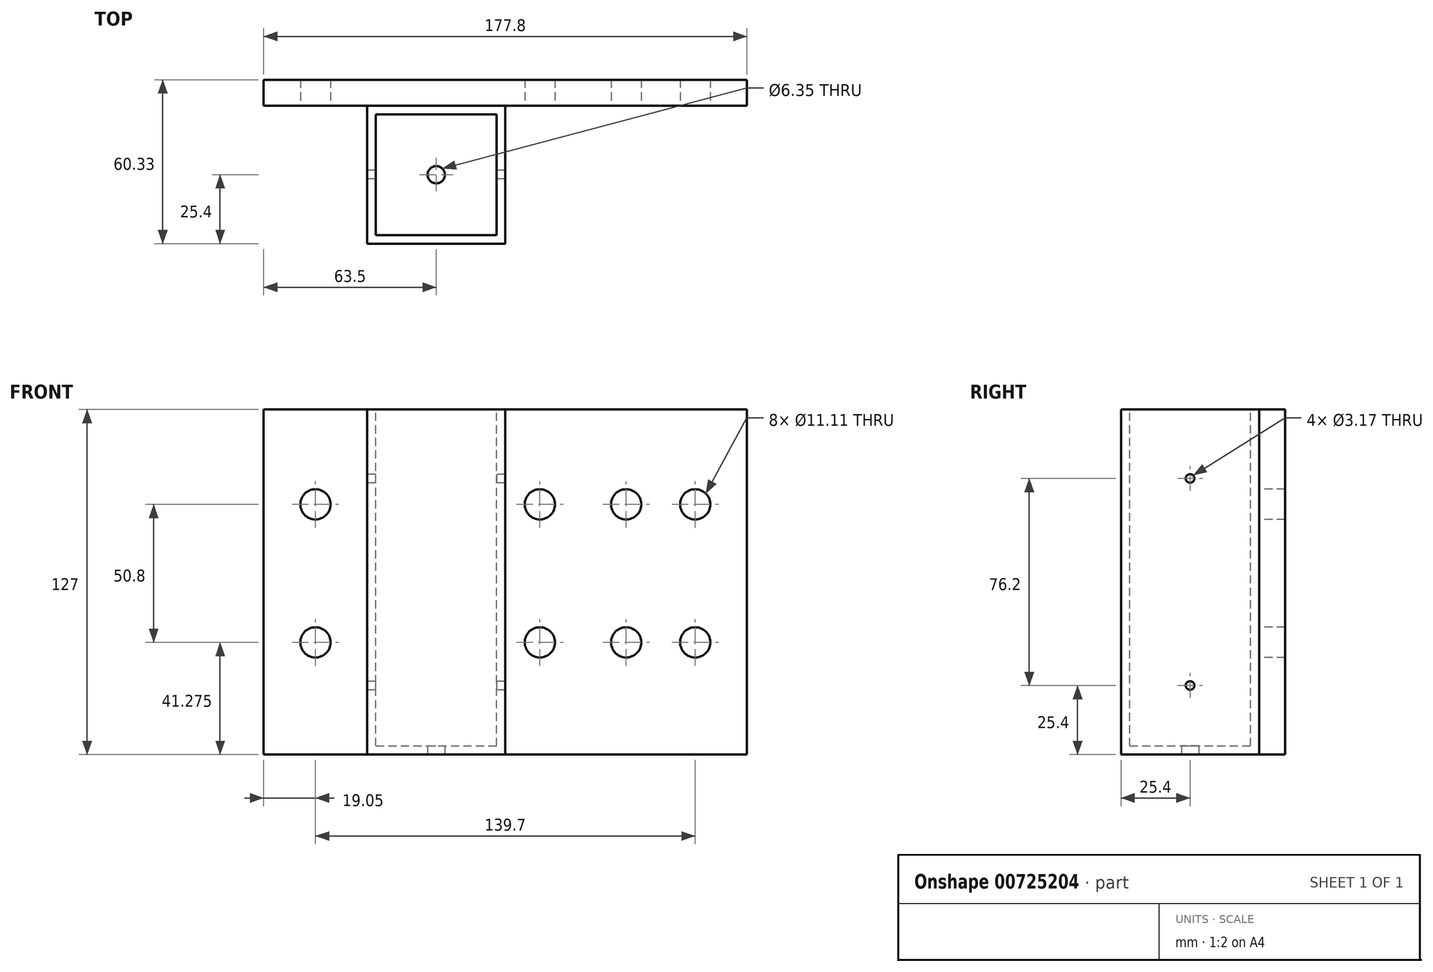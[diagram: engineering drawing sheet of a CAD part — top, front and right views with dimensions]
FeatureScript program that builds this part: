
annotation { "Feature Type Name" : "Feature", "Feature Type Description" : "" }
export const myFeature = defineFeature(function(context is Context, id is Id, definition is map)
    precondition{}
    {
        {
            var Q0;
            Q0=qCreatedBy(makeId("Front.planeOp"),FACE);
            var sketch = newSketch(context, id + "F0", { "sketchPlane" : qUnion([Q0])});
            skLineSegment(sketch, "E0.bottom", {"start": v(0, 0) * mm, "end": v(177.8, 0) * mm});
            skLineSegment(sketch, "E0.top", {"start": v(0, 127) * mm, "end": v(177.8, 127) * mm});
            skLineSegment(sketch, "E0.left", {"start": v(0, 0) * mm, "end": v(0, 127) * mm});
            skLineSegment(sketch, "E0.right", {"start": v(177.8, 0) * mm, "end": v(177.8, 127) * mm});
            skSolve(sketch);
        }
        {
            var Q0;
            Q0=makeQuery(id+"F0.imprint","IMPRINT",FACE,{"disambiguationData":[TD([[makeQuery(id+"F0.imprint","IMPRINT",EDGE,{"derivedFrom":sQuery(id+"F0.wireOp",EDGE,"E0.bottom")}),1.0]])]});
            extrude(context, id + "F1", {"entities" : qUnion([Q0]), "oppositeDirection" : true, "depth" : 9.52 * mm, "offsetDistance" : 25.4 * mm});
        }
        {
            var Q0;
            Q0=makeQuery(id+"F1.opExtrude","CAP_FACE",FACE,{"disambiguationData":[OSD([sQuery(id+"F0.wireOp",EDGE,"E0.bottom"),sQuery(id+"F0.wireOp",EDGE,"E0.top"),sQuery(id+"F0.wireOp",EDGE,"E0.left"),sQuery(id+"F0.wireOp",EDGE,"E0.right")])],"isStart":true});
            var sketch = newSketch(context, id + "F2", { "sketchPlane" : qUnion([Q0])});
            skLineSegment(sketch, "E1", {"start": v(177.8, 127) * mm, "end": v(177.8, 92.07) * mm});
            skLineSegment(sketch, "E2", {"start": v(177.8, 92.07) * mm, "end": v(177.8, 41.27) * mm});
            skLineSegment(sketch, "E3", {"start": v(177.8, 41.27) * mm, "end": v(177.8, 0) * mm});
            skLineSegment(sketch, "E4", {"start": v(177.8, 41.27) * mm, "end": v(0, 41.27) * mm});
            skLineSegment(sketch, "E5", {"start": v(177.8, 92.07) * mm, "end": v(0, 92.07) * mm});
            skLineSegment(sketch, "E6", {"start": v(177.8, 127) * mm, "end": v(158.75, 127) * mm});
            skLineSegment(sketch, "E7", {"start": v(158.75, 127) * mm, "end": v(158.75, 0) * mm});
            skLineSegment(sketch, "E8", {"start": v(158.75, 127) * mm, "end": v(133.35, 127) * mm});
            skLineSegment(sketch, "E9", {"start": v(101.6, 127) * mm, "end": v(101.6, 0) * mm});
            skLineSegment(sketch, "E10", {"start": v(133.35, 127) * mm, "end": v(133.35, 0) * mm});
            skPoint(sketch, "E11", {"position": v(101.6, 92.07) * mm});
            skPoint(sketch, "E12", {"position": v(133.35, 92.07) * mm});
            skPoint(sketch, "E13", {"position": v(158.75, 92.07) * mm});
            skPoint(sketch, "E14", {"position": v(158.75, 41.27) * mm});
            skPoint(sketch, "E15", {"position": v(133.35, 41.27) * mm});
            skPoint(sketch, "E16", {"position": v(101.6, 41.27) * mm});
            skLineSegment(sketch, "E17", {"start": v(0, 127) * mm, "end": v(19.05, 127) * mm});
            skLineSegment(sketch, "E18", {"start": v(19.05, 127) * mm, "end": v(19.05, 0) * mm});
            skPoint(sketch, "E19", {"position": v(19.05, 92.07) * mm});
            skPoint(sketch, "E20", {"position": v(19.05, 41.27) * mm});
            skSolve(sketch);
        }
        {
            var Q0;
            Q0=sQuery(id+"F2.wireOp",VERTEX,"9d8f6d40-7815-4581-81f3-3615b596abd9");
            var Q1;
            Q1=sQuery(id+"F2.wireOp",VERTEX,"E11");
            var Q2;
            Q2=sQuery(id+"F2.wireOp",VERTEX,"E12");
            var Q3;
            Q3=sQuery(id+"F2.wireOp",VERTEX,"E13");
            var Q4;
            Q4=sQuery(id+"F2.wireOp",VERTEX,"E14");
            var Q5;
            Q5=sQuery(id+"F2.wireOp",VERTEX,"E15");
            var Q6;
            Q6=sQuery(id+"F2.wireOp",VERTEX,"E16");
            var Q7;
            Q7=sQuery(id+"F2.wireOp",VERTEX,"e9cea253-7712-4655-bad3-f5c4aa77bfe9");
            var Q8;
            Q8=sQuery(id+"F2.wireOp",VERTEX,"E19");
            var Q9;
            Q9=sQuery(id+"F2.wireOp",VERTEX,"E20");
            var Q10;
            Q10=makeQuery(id+"F1.opExtrude","SWEPT_BODY",BODY,{"disambiguationData":[OSD([sQuery(id+"F0.wireOp",EDGE,"E0.bottom"),sQuery(id+"F0.wireOp",EDGE,"E0.top"),sQuery(id+"F0.wireOp",EDGE,"E0.left"),sQuery(id+"F0.wireOp",EDGE,"E0.right")])]});
            hole(context, id + "F3", {"style" : HoleStyle.SIMPLE, "endStyle" : HoleEndStyle.THROUGH, "holeDiameter" : 11.1 * mm, "majorDiameter" : 6.35 * mm, "isTappedThrough" : true, "tappedDepth" : 12.7 * mm, "tapClearance" : 3, "locations" : qUnion([Q0, Q1, Q2, Q3, Q4, Q5, Q6, Q7, Q8, Q9]), "scope" : qUnion([Q10])});
        }
        {
            var Q0;
            Q0=makeQuery(id+"F1.opExtrude","SWEPT_FACE",FACE,{"disambiguationData":[OSD([sQuery(id+"F0.wireOp",EDGE,"E0.top")])]});
            var sketch = newSketch(context, id + "F4", { "sketchPlane" : qUnion([Q0])});
            skLineSegment(sketch, "E21", {"start": v(0, 0) * mm, "end": v(19.05, 0) * mm});
            skLineSegment(sketch, "E22", {"start": v(19.05, 0) * mm, "end": v(38.1, 0) * mm});
            skLineSegment(sketch, "E23", {"start": v(38.1, 0) * mm, "end": v(88.9, 0) * mm});
            skLineSegment(sketch, "E24", {"start": v(88.9, 0) * mm, "end": v(88.9, -50.8) * mm});
            skLineSegment(sketch, "E25", {"start": v(88.9, -50.8) * mm, "end": v(38.1, -50.8) * mm});
            skLineSegment(sketch, "E26", {"start": v(38.1, -50.8) * mm, "end": v(38.1, 0) * mm});
            skLineSegment(sketch, "E27.0", {"start": v(41.28, -3.18) * mm, "end": v(85.73, -3.18) * mm});
            skLineSegment(sketch, "E27.1", {"start": v(41.27, -47.63) * mm, "end": v(41.27, -3.18) * mm});
            skLineSegment(sketch, "E27.2", {"start": v(85.73, -47.63) * mm, "end": v(41.27, -47.63) * mm});
            skLineSegment(sketch, "E27.3", {"start": v(85.73, -3.18) * mm, "end": v(85.73, -47.63) * mm});
            skSolve(sketch);
        }
        {
            var Q0;
            Q0=makeQuery(id+"F4.imprint","IMPRINT",FACE,{"disambiguationData":[TD([[makeQuery(id+"F4.imprint","IMPRINT",EDGE,{"derivedFrom":sQuery(id+"F4.wireOp",EDGE,"E23")}),-1.0]])]});
            extrude(context, id + "F5", {"entities" : qUnion([Q0]), "oppositeDirection" : true, "depth" : 127 * mm, "offsetDistance" : 25.4 * mm});
        }
        {
            var Q0;
            Q0=makeQuery(id+"F5.opExtrude","SWEPT_FACE",FACE,{"disambiguationData":[OSD([sQuery(id+"F4.wireOp",EDGE,"E26")])]});
            var sketch = newSketch(context, id + "F6", { "sketchPlane" : qUnion([Q0])});
            skLineSegment(sketch, "E28", {"start": v(25.4, 127) * mm, "end": v(25.4, 0) * mm});
            skLineSegment(sketch, "E29", {"start": v(25.4, 127) * mm, "end": v(25.4, 101.6) * mm});
            skLineSegment(sketch, "E30", {"start": v(25.4, 101.6) * mm, "end": v(25.4, 25.4) * mm});
            skSolve(sketch);
        }
        {
            var Q0;
            Q0=sQuery(id+"F6.wireOp",VERTEX,"E30.start");
            var Q1;
            Q1=sQuery(id+"F6.wireOp",VERTEX,"E30.end");
            var Q2;
            Q2=makeQuery(id+"F5.opExtrude","SWEPT_BODY",BODY,{"disambiguationData":[OSD([sQuery(id+"F4.wireOp",EDGE,"E23"),sQuery(id+"F4.wireOp",EDGE,"E24"),sQuery(id+"F4.wireOp",EDGE,"E25"),sQuery(id+"F4.wireOp",EDGE,"E26"),sQuery(id+"F4.wireOp",EDGE,"E27.0"),sQuery(id+"F4.wireOp",EDGE,"E27.1"),sQuery(id+"F4.wireOp",EDGE,"E27.2"),sQuery(id+"F4.wireOp",EDGE,"E27.3")])]});
            hole(context, id + "F7", {"style" : HoleStyle.SIMPLE, "endStyle" : HoleEndStyle.THROUGH, "holeDiameter" : 3.17 * mm, "majorDiameter" : 6.35 * mm, "isTappedThrough" : true, "tappedDepth" : 12.7 * mm, "tapClearance" : 3, "locations" : qUnion([Q0, Q1]), "scope" : qUnion([Q2])});
        }
        {
            var Q0;
            Q0=makeQuery(id+"F5.opExtrude","CAP_FACE",FACE,{"disambiguationData":[OSD([sQuery(id+"F4.wireOp",EDGE,"E23"),sQuery(id+"F4.wireOp",EDGE,"E24"),sQuery(id+"F4.wireOp",EDGE,"E25"),sQuery(id+"F4.wireOp",EDGE,"E26"),sQuery(id+"F4.wireOp",EDGE,"E27.0"),sQuery(id+"F4.wireOp",EDGE,"E27.1"),sQuery(id+"F4.wireOp",EDGE,"E27.2"),sQuery(id+"F4.wireOp",EDGE,"E27.3")])],"isStart":false});
            var sketch = newSketch(context, id + "F8", { "sketchPlane" : qUnion([Q0])});
            skLineSegment(sketch, "E31.bottom", {"start": v(41.27, 47.63) * mm, "end": v(85.73, 47.63) * mm});
            skLineSegment(sketch, "E31.top", {"start": v(41.27, 3.18) * mm, "end": v(85.73, 3.18) * mm});
            skLineSegment(sketch, "E31.left", {"start": v(41.27, 47.63) * mm, "end": v(41.27, 3.18) * mm});
            skLineSegment(sketch, "E31.right", {"start": v(85.73, 47.63) * mm, "end": v(85.73, 3.18) * mm});
            skLineSegment(sketch, "E32", {"start": v(63.5, 47.63) * mm, "end": v(63.5, 3.18) * mm});
            skPoint(sketch, "E33", {"position": v(63.5, 25.4) * mm});
            skSolve(sketch);
        }
        {
            var Q0;
            {var subQ0=sQuery(id+"F8.wireOp",EDGE,"E31.right");Q0=makeQuery(id+"F8.imprint","IMPRINT",FACE,{"disambiguationData":[TD([[makeQuery(id+"F8.imprint","IMPRINT",EDGE,{"derivedFrom":subQ0}),1.0]])]});}
            var Q1;
            {var subQ0=sQuery(id+"F8.wireOp",EDGE,"E31.left");Q1=makeQuery(id+"F8.imprint","IMPRINT",FACE,{"disambiguationData":[TD([[makeQuery(id+"F8.imprint","IMPRINT",EDGE,{"derivedFrom":subQ0}),1.0]])]});}
            extrude(context, id + "F9", {"entities" : qUnion([Q0, Q1]), "operationType" : NewBodyOperationType.ADD, "oppositeDirection" : true, "depth" : 3.17 * mm, "offsetDistance" : 25.4 * mm});
        }
        {
            var Q0;
            Q0=sQuery(id+"F8.wireOp",VERTEX,"E33");
            var Q1;
            Q1=makeQuery(id+"F5.opExtrude","SWEPT_BODY",BODY,{"disambiguationData":[OSD([sQuery(id+"F4.wireOp",EDGE,"E23"),sQuery(id+"F4.wireOp",EDGE,"E24"),sQuery(id+"F4.wireOp",EDGE,"E25"),sQuery(id+"F4.wireOp",EDGE,"E26"),sQuery(id+"F4.wireOp",EDGE,"E27.0"),sQuery(id+"F4.wireOp",EDGE,"E27.1"),sQuery(id+"F4.wireOp",EDGE,"E27.2"),sQuery(id+"F4.wireOp",EDGE,"E27.3")])]});
            hole(context, id + "F10", {"style" : HoleStyle.SIMPLE, "endStyle" : HoleEndStyle.THROUGH, "holeDiameter" : 6.35 * mm, "majorDiameter" : 6.35 * mm, "isTappedThrough" : true, "tappedDepth" : 12.7 * mm, "tapClearance" : 3, "locations" : qUnion([Q0]), "scope" : qUnion([Q1])});
        }
    });
